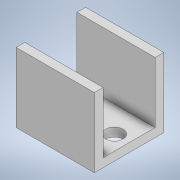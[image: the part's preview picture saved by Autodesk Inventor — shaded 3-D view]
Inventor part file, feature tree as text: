
AUTODESK INVENTOR PART (.ipt)
format: ipt  version: 2021 (Build 250183000, 183)  size: 113,664 bytes
history: native  units: in
note: dims shown in document units (in); Inventor stores cm internally (conversion verified against a paired STEP export)
features: extrude x2, sketch x2, mirror x1, projected_geometry x1
ambient origin geometry x8: Origin, YZ Plane, XZ Plane, XY Plane, X Axis, Y Axis, Z Axis, Center Point
bodies: Solid1 (feature_tree)
feature tree (6):
  extrude  "Extrusion1"  Depth=0.5in
  extrude  "Extrusion2"  Depth=0.375in
  mirror  "Mirror1"
  sketch  "Sketch2"  dims[d0=0.5in d1=0.5in]
  sketch  "Sketch3"  dims[d2=0.375in d3=0.375in d4=0.5625in d5=0.0in d6=0.125in d7=0.175in d8=0.0in d9=0.0in]
  projected_geometry  "Projected Loop1"
